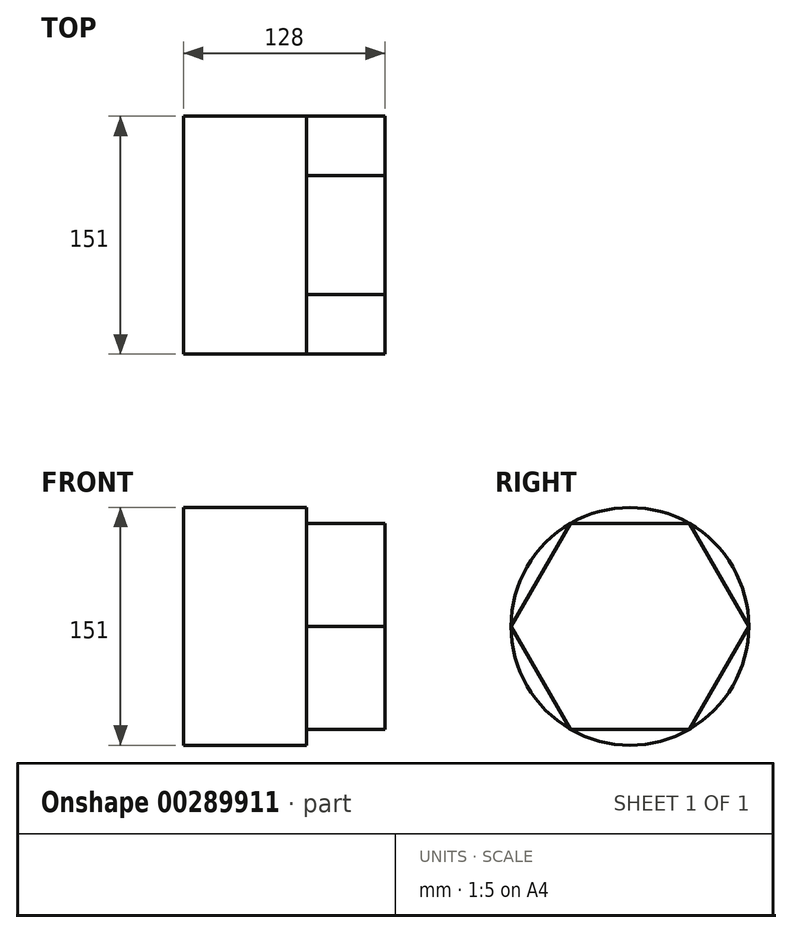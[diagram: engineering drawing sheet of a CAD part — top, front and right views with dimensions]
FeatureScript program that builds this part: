
annotation { "Feature Type Name" : "Feature", "Feature Type Description" : "" }
export const myFeature = defineFeature(function(context is Context, id is Id, definition is map)
    precondition{}
    {
        {
            var Q0;
            Q0=qCreatedBy(makeId("Right.planeOp"),FACE);
            var sketch = newSketch(context, id + "F0", { "sketchPlane" : qUnion([Q0])});
            skCircle(sketch, "E0", {"center": v(0, 0) * mm, "radius": 75.5 * mm});
            skSolve(sketch);
        }
        {
            var Q0;
            Q0=qSketchRegion(id+"F0",true);
            extrude(context, id + "F1", {"entities" : qUnion([Q0]), "depth" : 128 * mm});
        }
        {
            var Q0;
            Q0=makeQuery(id+"F1.opExtrude","CAP_FACE",FACE,{"disambiguationData":[OSD([sQuery(id+"F0.wireOp",EDGE,"E0")])],"isStart":false});
            var sketch = newSketch(context, id + "F2", { "sketchPlane" : qUnion([Q0])});
            skCircle(sketch, "E1.cCircle", {"center": v(0, 0) * mm, "radius": 75.5 * mm, "construction": true});
            skLineSegment(sketch, "E1.0", {"start": v(-37.75, 65.38) * mm, "end": v(37.75, 65.38) * mm});
            skLineSegment(sketch, "E1.1", {"start": v(37.75, 65.38) * mm, "end": v(75.5, 0) * mm});
            skLineSegment(sketch, "E1.2", {"start": v(75.5, 0) * mm, "end": v(37.75, -65.38) * mm});
            skLineSegment(sketch, "E1.3", {"start": v(37.75, -65.38) * mm, "end": v(-37.75, -65.38) * mm});
            skLineSegment(sketch, "E1.4", {"start": v(-37.75, -65.38) * mm, "end": v(-75.5, 0) * mm});
            skLineSegment(sketch, "E1.5", {"start": v(-75.5, 0) * mm, "end": v(-37.75, 65.38) * mm});
            skSolve(sketch);
        }
        {
            var Q0;
            {var subQ0=sQuery(id+"F2.wireOp",EDGE,"E1.5");Q0=makeQuery(id+"F2.imprint","IMPRINT",FACE,{"disambiguationData":[TD([[makeQuery(id+"F2.imprint","IMPRINT",EDGE,{"derivedFrom":subQ0}),1.0]])]});}
            var Q1;
            {var subQ0=sQuery(id+"F2.wireOp",EDGE,"E1.0");Q1=makeQuery(id+"F2.imprint","IMPRINT",FACE,{"disambiguationData":[TD([[makeQuery(id+"F2.imprint","IMPRINT",EDGE,{"derivedFrom":subQ0}),1.0]])]});}
            var Q2;
            {var subQ0=sQuery(id+"F2.wireOp",EDGE,"E1.1");Q2=makeQuery(id+"F2.imprint","IMPRINT",FACE,{"disambiguationData":[TD([[makeQuery(id+"F2.imprint","IMPRINT",EDGE,{"derivedFrom":subQ0}),1.0]])]});}
            var Q3;
            {var subQ0=sQuery(id+"F2.wireOp",EDGE,"E1.2");Q3=makeQuery(id+"F2.imprint","IMPRINT",FACE,{"disambiguationData":[TD([[makeQuery(id+"F2.imprint","IMPRINT",EDGE,{"derivedFrom":subQ0}),1.0]])]});}
            var Q4;
            {var subQ0=sQuery(id+"F2.wireOp",EDGE,"E1.3");Q4=makeQuery(id+"F2.imprint","IMPRINT",FACE,{"disambiguationData":[TD([[makeQuery(id+"F2.imprint","IMPRINT",EDGE,{"derivedFrom":subQ0}),1.0]])]});}
            var Q5;
            {var subQ0=sQuery(id+"F2.wireOp",EDGE,"E1.4");Q5=makeQuery(id+"F2.imprint","IMPRINT",FACE,{"disambiguationData":[TD([[makeQuery(id+"F2.imprint","IMPRINT",EDGE,{"derivedFrom":subQ0}),1.0]])]});}
            extrude(context, id + "F3", {"entities" : qUnion([Q0, Q1, Q2, Q3, Q4, Q5]), "operationType" : NewBodyOperationType.REMOVE, "oppositeDirection" : true, "depth" : 50 * mm});
        }
        {
            var Q0;
            Q0=makeQuery(id+"F1.opExtrude","SWEPT_BODY",BODY,{"disambiguationData":[OSD([sQuery(id+"F0.wireOp",EDGE,"E0")])]});
            transform(context, id + "F4", {"entities" : qUnion([Q0]), "transformType" : TransformType.TRANSLATION_3D, "dx" : 0 * mm, "dy" : 0 * mm, "dz" : 0 * mm, "makeCopy" : false});
        }
    });
